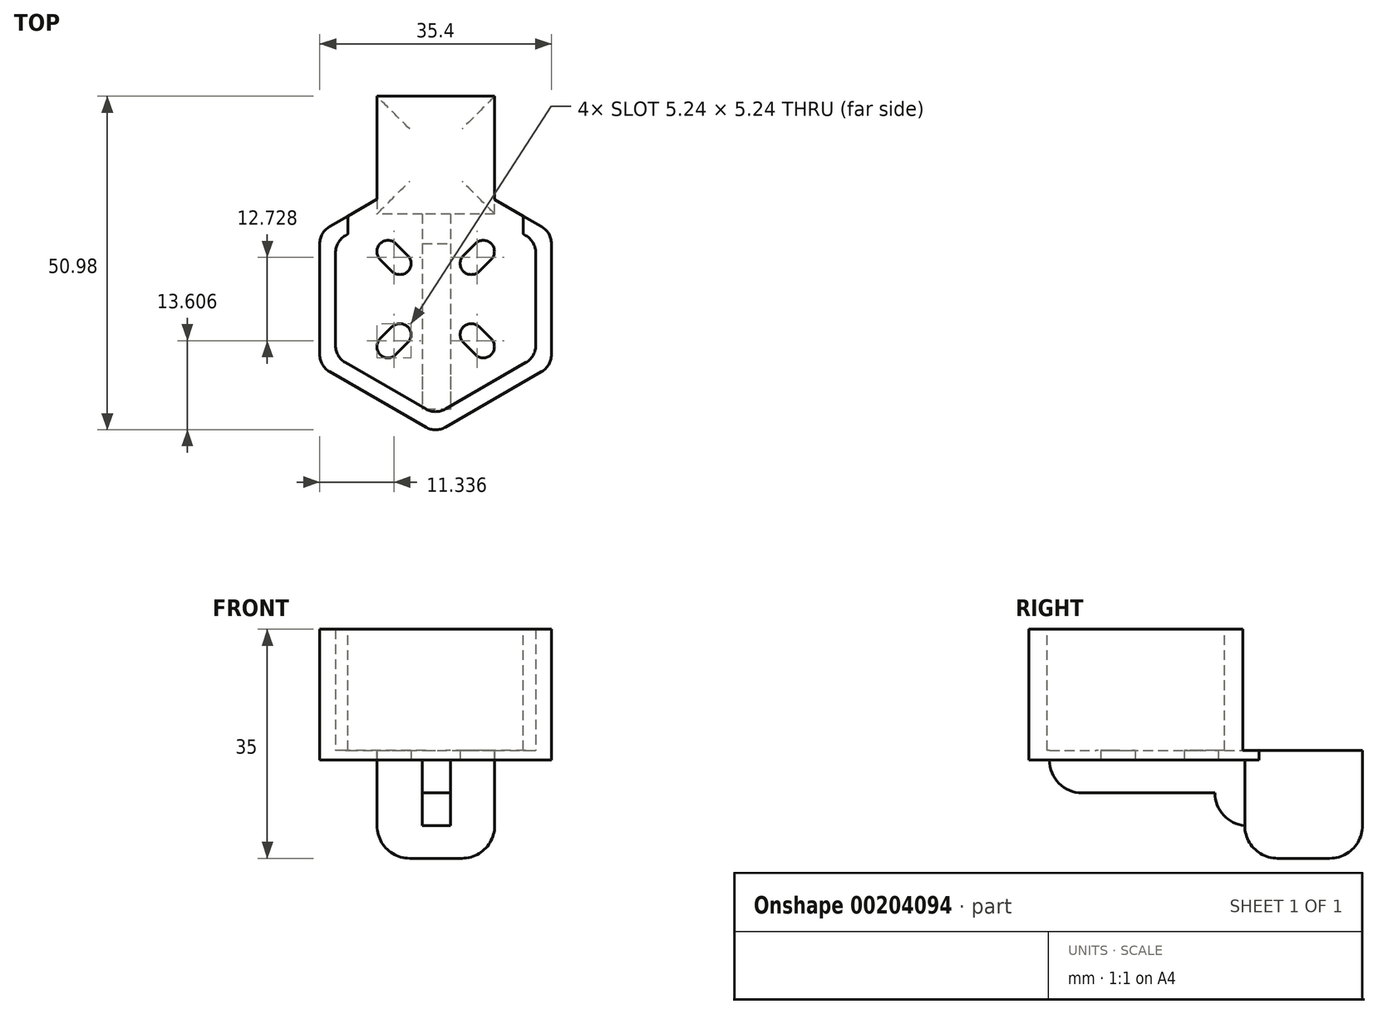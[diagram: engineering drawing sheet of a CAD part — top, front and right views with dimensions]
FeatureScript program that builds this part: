
annotation { "Feature Type Name" : "Feature", "Feature Type Description" : "" }
export const myFeature = defineFeature(function(context is Context, id is Id, definition is map)
    precondition{}
    {
        {
            var Q0;
            Q0=qCreatedBy(makeId("Top.planeOp"),FACE);
            var sketch = newSketch(context, id + "F0", { "sketchPlane" : qUnion([Q0])});
            skPoint(sketch, "E0", {"position": v(0, 0) * mm});
            skLineSegment(sketch, "E1", {"start": v(-20.56, -20.56) * mm, "end": v(20.56, 20.56) * mm, "construction": true});
            skLineSegment(sketch, "E2", {"start": v(-19.47, 19.47) * mm, "end": v(19.47, -19.47) * mm, "construction": true});
            skArc(sketch, "E3", {"start": v(-6.08, 8.49) * mm, "mid": v(-8.49, 8.49) * mm, "end": v(-8.49, 6.08) * mm});
            skArc(sketch, "E4", {"start": v(-6.65, 4.24) * mm, "mid": v(-4.24, 4.24) * mm, "end": v(-4.24, 6.65) * mm});
            skLineSegment(sketch, "E5", {"start": v(-6.08, 8.49) * mm, "end": v(-4.24, 6.65) * mm});
            skLineSegment(sketch, "E6", {"start": v(-8.49, 6.08) * mm, "end": v(-6.65, 4.24) * mm});
            skLineSegment(sketch, "E7.MirrorCS", {"start": v(-8.49, -6.08) * mm, "end": v(-6.65, -4.24) * mm});
            skArc(sketch, "E8.MirrorCS", {"start": v(-6.08, -8.49) * mm, "mid": v(-8.49, -8.49) * mm, "end": v(-8.49, -6.08) * mm});
            skArc(sketch, "E9.MirrorCS", {"start": v(-6.65, -4.24) * mm, "mid": v(-4.24, -4.24) * mm, "end": v(-4.24, -6.65) * mm});
            skLineSegment(sketch, "E10.MirrorCS", {"start": v(-6.08, -8.49) * mm, "end": v(-4.24, -6.65) * mm});
            skLineSegment(sketch, "E11.MirrorCS", {"start": v(6.08, -8.49) * mm, "end": v(4.24, -6.65) * mm});
            skLineSegment(sketch, "E12.MirrorCS", {"start": v(8.49, -6.08) * mm, "end": v(6.65, -4.24) * mm});
            skLineSegment(sketch, "E13.MirrorCS", {"start": v(6.08, 8.49) * mm, "end": v(4.24, 6.65) * mm});
            skArc(sketch, "E14.MirrorCS", {"start": v(6.65, -4.24) * mm, "mid": v(4.24, -4.24) * mm, "end": v(4.24, -6.65) * mm});
            skLineSegment(sketch, "E15.MirrorCS", {"start": v(8.49, 6.08) * mm, "end": v(6.65, 4.24) * mm});
            skArc(sketch, "E16.MirrorCS", {"start": v(6.08, -8.49) * mm, "mid": v(8.49, -8.49) * mm, "end": v(8.49, -6.08) * mm});
            skArc(sketch, "E17.MirrorCS", {"start": v(6.08, 8.49) * mm, "mid": v(8.49, 8.49) * mm, "end": v(8.49, 6.08) * mm});
            skArc(sketch, "E18.MirrorCS", {"start": v(6.65, 4.24) * mm, "mid": v(4.24, 4.24) * mm, "end": v(4.24, 6.65) * mm});
            skCircle(sketch, "E19.cCircle", {"center": v(0, 0) * mm, "radius": 15.3 * mm, "construction": true});
            skLineSegment(sketch, "E19.0", {"start": v(15.3, -8.83) * mm, "end": v(0, -17.67) * mm});
            skLineSegment(sketch, "E19.1", {"start": v(0, -17.67) * mm, "end": v(-15.3, -8.83) * mm});
            skLineSegment(sketch, "E19.2", {"start": v(-15.3, -8.83) * mm, "end": v(-15.3, 8.83) * mm});
            skLineSegment(sketch, "E19.3", {"start": v(-15.3, 8.83) * mm, "end": v(0, 17.67) * mm});
            skLineSegment(sketch, "E19.4", {"start": v(0, 17.67) * mm, "end": v(15.3, 8.83) * mm});
            skLineSegment(sketch, "E19.5", {"start": v(15.3, 8.83) * mm, "end": v(15.3, -8.83) * mm});
            skPoint(sketch, "E19.0.midPoint", {"position": v(7.65, -13.25) * mm});
            skLineSegment(sketch, "E20.0", {"start": v(-17.7, -10.22) * mm, "end": v(-17.7, 10.22) * mm});
            skLineSegment(sketch, "E20.1", {"start": v(0, 20.44) * mm, "end": v(17.7, 10.22) * mm});
            skLineSegment(sketch, "E20.2", {"start": v(17.7, 10.22) * mm, "end": v(17.7, -10.22) * mm});
            skLineSegment(sketch, "E20.3", {"start": v(-17.7, 10.22) * mm, "end": v(0, 20.44) * mm});
            skLineSegment(sketch, "E20.4", {"start": v(17.7, -10.22) * mm, "end": v(0, -20.44) * mm});
            skLineSegment(sketch, "E20.5", {"start": v(0, -20.44) * mm, "end": v(-17.7, -10.22) * mm});
            skSolve(sketch);
        }
        {
            var Q0;
            Q0=makeQuery(id+"F0.imprint","IMPRINT",FACE,{"disambiguationData":[TD([[makeQuery(id+"F0.imprint","IMPRINT",EDGE,{"derivedFrom":sQuery(id+"F0.wireOp",EDGE,"E3")}),-1.0]])]});
            extrude(context, id + "F1", {"entities" : qUnion([Q0]), "depth" : 1.5 * mm});
        }
        {
            var Q0;
            Q0=makeQuery(id+"F0.imprint","IMPRINT",FACE,{"disambiguationData":[TD([[makeQuery(id+"F0.imprint","IMPRINT",EDGE,{"derivedFrom":sQuery(id+"F0.wireOp",EDGE,"E19.0")}),1.0]])]});
            extrude(context, id + "F2", {"entities" : qUnion([Q0]), "operationType" : NewBodyOperationType.ADD, "depth" : 20 * mm});
        }
        {
            var Q0;
            Q0=qCreatedBy(makeId("Front.planeOp"),FACE);
            cPlane(context, id + "F3", {"entities" : qUnion([Q0]), "cplaneType" : CPlaneType.OFFSET, "offset" : 25 * mm, "oppositeDirection" : true, "width" : 150 * mm, "height" : 150 * mm});
        }
        {
            var Q0;
            Q0=qCreatedBy(id+"F3.planeOp",FACE);
            var sketch = newSketch(context, id + "F4", { "sketchPlane" : qUnion([Q0])});
            skLineSegment(sketch, "E21.bottom", {"start": v(-13.4, 1.5) * mm, "end": v(13.4, 1.5) * mm});
            skLineSegment(sketch, "E21.top", {"start": v(-13.4, 21.94) * mm, "end": v(13.4, 21.94) * mm});
            skLineSegment(sketch, "E21.left", {"start": v(-13.4, 1.5) * mm, "end": v(-13.4, 21.94) * mm});
            skLineSegment(sketch, "E21.right", {"start": v(13.4, 1.5) * mm, "end": v(13.4, 21.94) * mm});
            skPoint(sketch, "E21.middle", {"position": v(0, 11.72) * mm});
            skSolve(sketch);
        }
        {
            var Q0;
            Q0=makeQuery(id+"F4.imprint","IMPRINT",FACE,{"disambiguationData":[TD([[makeQuery(id+"F4.imprint","IMPRINT",EDGE,{"derivedFrom":sQuery(id+"F4.wireOp",EDGE,"E21.bottom")}),1.0]])]});
            extrude(context, id + "F5", {"entities" : qUnion([Q0]), "operationType" : NewBodyOperationType.REMOVE, "depth" : 26 * mm});
        }
        {
            var Q0;
            Q0=makeQuery(id+"F2.opExtrude","SWEPT_EDGE",EDGE,{"disambiguationData":[OSD([sQuery(id+"F0.wireOp",EDGE,"E20.1"),sQuery(id+"F0.wireOp",EDGE,"E20.2")])]});
            var Q1;
            Q1=makeQuery(id+"F2.opExtrude","SWEPT_EDGE",EDGE,{"disambiguationData":[OSD([sQuery(id+"F0.wireOp",EDGE,"E20.0"),sQuery(id+"F0.wireOp",EDGE,"E20.3")])]});
            var Q2;
            Q2=makeQuery(id+"F2.opExtrude","SWEPT_EDGE",EDGE,{"disambiguationData":[OSD([sQuery(id+"F0.wireOp",EDGE,"E20.0"),sQuery(id+"F0.wireOp",EDGE,"E20.5")])]});
            var Q3;
            Q3=makeQuery(id+"F2.opExtrude","SWEPT_EDGE",EDGE,{"disambiguationData":[OSD([sQuery(id+"F0.wireOp",EDGE,"E20.4"),sQuery(id+"F0.wireOp",EDGE,"E20.5")])]});
            var Q4;
            Q4=makeQuery(id+"F2.opExtrude","SWEPT_EDGE",EDGE,{"disambiguationData":[OSD([sQuery(id+"F0.wireOp",EDGE,"E20.2"),sQuery(id+"F0.wireOp",EDGE,"E20.4")])]});
            var Q5;
            Q5=makeQuery(id+"F2.opExtrude","SWEPT_EDGE",EDGE,{"disambiguationData":[OSD([sQuery(id+"F0.wireOp",EDGE,"E19.4"),sQuery(id+"F0.wireOp",EDGE,"E19.5")])]});
            var Q6;
            Q6=makeQuery(id+"F2.opExtrude","SWEPT_EDGE",EDGE,{"disambiguationData":[OSD([sQuery(id+"F0.wireOp",EDGE,"E19.0"),sQuery(id+"F0.wireOp",EDGE,"E19.5")])]});
            var Q7;
            Q7=makeQuery(id+"F2.opExtrude","SWEPT_EDGE",EDGE,{"disambiguationData":[OSD([sQuery(id+"F0.wireOp",EDGE,"E19.0"),sQuery(id+"F0.wireOp",EDGE,"E19.1")])]});
            var Q8;
            Q8=makeQuery(id+"F2.opExtrude","SWEPT_EDGE",EDGE,{"disambiguationData":[OSD([sQuery(id+"F0.wireOp",EDGE,"E19.1"),sQuery(id+"F0.wireOp",EDGE,"E19.2")])]});
            var Q9;
            Q9=makeQuery(id+"F2.opExtrude","SWEPT_EDGE",EDGE,{"disambiguationData":[OSD([sQuery(id+"F0.wireOp",EDGE,"E19.2"),sQuery(id+"F0.wireOp",EDGE,"E19.3")])]});
            fillet(context, id + "F6", {"entities" : qUnion([Q0, Q1, Q2, Q3, Q4, Q5, Q6, Q7, Q8, Q9]), "radius" : 3 * mm, "tangentPropagation" : true, "allowEdgeOverflow" : false});
        }
        {
            var Q0;
            Q0=makeQuery(id+"F1.opExtrude","CAP_EDGE",EDGE,{"disambiguationData":[OSD([sQuery(id+"F0.wireOp",EDGE,"E19.3")])],"isStart":false});
            var Q1;
            Q1=makeQuery(id+"F2.opExtrude","SWEPT_EDGE",EDGE,{"disambiguationData":[OSD([sQuery(id+"F0.wireOp",EDGE,"E20.1"),sQuery(id+"F0.wireOp",EDGE,"E20.3")])]});
            fillet(context, id + "F7", {"entities" : qUnion([Q0, Q1]), "radius" : 0.5 * mm, "tangentPropagation" : true, "allowEdgeOverflow" : false});
        }
        {
            var Q0;
            Q0=makeQuery(id+"F5.boolean.opBoolean","MERGE",FACE,{"derivedFrom":[makeQuery(id+"F1.opExtrude","CAP_FACE",FACE,{"disambiguationData":[OSD([sQuery(id+"F0.wireOp",EDGE,"E3"),sQuery(id+"F0.wireOp",EDGE,"E4"),sQuery(id+"F0.wireOp",EDGE,"E5"),sQuery(id+"F0.wireOp",EDGE,"E6"),sQuery(id+"F0.wireOp",EDGE,"E7.MirrorCS"),sQuery(id+"F0.wireOp",EDGE,"E8.MirrorCS"),sQuery(id+"F0.wireOp",EDGE,"E9.MirrorCS"),sQuery(id+"F0.wireOp",EDGE,"E10.MirrorCS"),sQuery(id+"F0.wireOp",EDGE,"E11.MirrorCS"),sQuery(id+"F0.wireOp",EDGE,"E12.MirrorCS"),sQuery(id+"F0.wireOp",EDGE,"E13.MirrorCS"),sQuery(id+"F0.wireOp",EDGE,"E14.MirrorCS"),sQuery(id+"F0.wireOp",EDGE,"E15.MirrorCS"),sQuery(id+"F0.wireOp",EDGE,"E16.MirrorCS"),sQuery(id+"F0.wireOp",EDGE,"E17.MirrorCS"),sQuery(id+"F0.wireOp",EDGE,"E18.MirrorCS"),sQuery(id+"F0.wireOp",EDGE,"E19.0"),sQuery(id+"F0.wireOp",EDGE,"E19.1"),sQuery(id+"F0.wireOp",EDGE,"E19.2"),sQuery(id+"F0.wireOp",EDGE,"E19.3"),sQuery(id+"F0.wireOp",EDGE,"E19.4"),sQuery(id+"F0.wireOp",EDGE,"E19.5")])],"isStart":false}),makeQuery(id+"F5.opExtrude","SWEPT_FACE",FACE,{"disambiguationData":[OSD([sQuery(id+"F4.wireOp",EDGE,"E21.bottom")])]})]});
            var sketch = newSketch(context, id + "F8", { "sketchPlane" : qUnion([Q0])});
            skLineSegment(sketch, "E22.bottom", {"start": v(-8.97, 11.01) * mm, "end": v(9.03, 11.01) * mm});
            skLineSegment(sketch, "E22.top", {"start": v(-8.97, 31.01) * mm, "end": v(9.03, 31.01) * mm});
            skLineSegment(sketch, "E22.left", {"start": v(-8.97, 11.01) * mm, "end": v(-8.97, 31.01) * mm});
            skLineSegment(sketch, "E22.right", {"start": v(9.03, 11.01) * mm, "end": v(9.03, 31.01) * mm});
            skSolve(sketch);
        }
        {
            var Q0;
            {var subQ5=sQuery(id+"F8.wireOp",EDGE,"E22.top");Q0=makeQuery(id+"F8.imprint","IMPRINT",FACE,{"disambiguationData":[TD([[makeQuery(id+"F8.imprint","IMPRINT",EDGE,{"derivedFrom":subQ5}),-1.0]])]});}
            extrude(context, id + "F9", {"entities" : qUnion([Q0]), "operationType" : NewBodyOperationType.ADD, "oppositeDirection" : true, "depth" : 1.5 * mm});
        }
        {
            var Q0;
            {var subQ0=sQuery(id+"F0.wireOp",EDGE,"E20.3");var subQ1=sQuery(id+"F0.wireOp",EDGE,"E20.1");var subQ2=sQuery(id+"F0.wireOp",EDGE,"E19.5");var subQ3=sQuery(id+"F0.wireOp",EDGE,"E19.4");var subQ4=sQuery(id+"F0.wireOp",EDGE,"E19.3");var subQ5=sQuery(id+"F0.wireOp",EDGE,"E19.2");var subQ6=sQuery(id+"F0.wireOp",EDGE,"E19.1");var subQ7=sQuery(id+"F0.wireOp",EDGE,"E19.0");var subQ8=sQuery(id+"F0.wireOp",EDGE,"E18.MirrorCS");var subQ9=sQuery(id+"F0.wireOp",EDGE,"E17.MirrorCS");var subQ10=sQuery(id+"F0.wireOp",EDGE,"E16.MirrorCS");var subQ11=sQuery(id+"F0.wireOp",EDGE,"E15.MirrorCS");var subQ12=sQuery(id+"F0.wireOp",EDGE,"E14.MirrorCS");var subQ13=sQuery(id+"F0.wireOp",EDGE,"E13.MirrorCS");var subQ14=sQuery(id+"F0.wireOp",EDGE,"E12.MirrorCS");var subQ15=sQuery(id+"F0.wireOp",EDGE,"E11.MirrorCS");var subQ16=sQuery(id+"F0.wireOp",EDGE,"E10.MirrorCS");var subQ17=sQuery(id+"F0.wireOp",EDGE,"E9.MirrorCS");var subQ18=sQuery(id+"F0.wireOp",EDGE,"E8.MirrorCS");var subQ19=sQuery(id+"F0.wireOp",EDGE,"E7.MirrorCS");var subQ20=sQuery(id+"F0.wireOp",EDGE,"E6");var subQ21=sQuery(id+"F0.wireOp",EDGE,"E5");var subQ22=sQuery(id+"F0.wireOp",EDGE,"E4");var subQ23=sQuery(id+"F0.wireOp",EDGE,"E3");Q0=makeQuery(id+"F9.boolean.opBoolean","MERGE",FACE,{"derivedFrom":[makeQuery(id+"F2.boolean.opBoolean","MERGE",FACE,{"derivedFrom":[makeQuery(id+"F1.opExtrude","CAP_FACE",FACE,{"disambiguationData":[OSD([subQ23,subQ22,subQ21,subQ20,subQ19,subQ18,subQ17,subQ16,subQ15,subQ14,subQ13,subQ12,subQ11,subQ10,subQ9,subQ8,subQ7,subQ6,subQ5,subQ4,subQ3,subQ2])],"isStart":true}),makeQuery(id+"F2.opExtrude","CAP_FACE",FACE,{"disambiguationData":[OSD([subQ7,subQ6,subQ5,subQ4,subQ3,subQ2,sQuery(id+"F0.wireOp",EDGE,"E20.0"),subQ1,sQuery(id+"F0.wireOp",EDGE,"E20.2"),subQ0,sQuery(id+"F0.wireOp",EDGE,"E20.4"),sQuery(id+"F0.wireOp",EDGE,"E20.5")])],"isStart":true})]}),makeQuery(id+"F9.opExtrude","CAP_FACE",FACE,{"disambiguationData":[OSD([subQ23,subQ22,subQ21,subQ20,subQ19,subQ18,subQ17,subQ16,subQ15,subQ14,subQ13,subQ12,subQ11,subQ10,subQ9,subQ8,subQ7,subQ6,subQ5,subQ4,subQ3,subQ2,subQ1,subQ0,sQuery(id+"F4.wireOp",EDGE,"E21.bottom"),sQuery(id+"F8.wireOp",EDGE,"E22.top"),sQuery(id+"F8.wireOp",EDGE,"E22.left"),sQuery(id+"F8.wireOp",EDGE,"E22.right")])],"isStart":false})]});}
            var sketch = newSketch(context, id + "F10", { "sketchPlane" : qUnion([Q0])});
            skLineSegment(sketch, "E23.bottom", {"start": v(9.03, -31.01) * mm, "end": v(-8.97, -31.01) * mm});
            skLineSegment(sketch, "E23.top", {"start": v(9.03, -13.01) * mm, "end": v(-8.97, -13.01) * mm});
            skLineSegment(sketch, "E23.left", {"start": v(9.03, -31.01) * mm, "end": v(9.03, -13.01) * mm});
            skLineSegment(sketch, "E23.right", {"start": v(-8.97, -31.01) * mm, "end": v(-8.97, -13.01) * mm});
            skSolve(sketch);
        }
        {
            var Q0;
            Q0 = qSketchRegion(id + "F10", true);
            extrude(context, id + "F11", {"entities" : qUnion([Q0]), "operationType" : NewBodyOperationType.ADD, "depth" : 15 * mm});
        }
        {
            var Q0;
            Q0=makeQuery(id+"F11.opExtrude","CAP_EDGE",EDGE,{"disambiguationData":[OSD([sQuery(id+"F10.wireOp",EDGE,"E23.left")])],"isStart":false});
            var Q1;
            Q1=makeQuery(id+"F11.opExtrude","CAP_EDGE",EDGE,{"disambiguationData":[OSD([sQuery(id+"F10.wireOp",EDGE,"E23.top")])],"isStart":false});
            var Q2;
            Q2=makeQuery(id+"F11.opExtrude","CAP_EDGE",EDGE,{"disambiguationData":[OSD([sQuery(id+"F10.wireOp",EDGE,"E23.right")])],"isStart":false});
            var Q3;
            Q3=makeQuery(id+"F11.opExtrude","CAP_EDGE",EDGE,{"disambiguationData":[OSD([sQuery(id+"F10.wireOp",EDGE,"E23.bottom")])],"isStart":false});
            fillet(context, id + "F12", {"entities" : qUnion([Q0, Q1, Q2, Q3]), "radius" : 5 * mm, "tangentPropagation" : true, "allowEdgeOverflow" : false});
        }
        {
            var Q0;
            {var subQ0=sQuery(id+"F0.wireOp",EDGE,"E20.3");var subQ1=sQuery(id+"F0.wireOp",EDGE,"E20.1");var subQ2=sQuery(id+"F0.wireOp",EDGE,"E19.5");var subQ3=sQuery(id+"F0.wireOp",EDGE,"E19.4");var subQ4=sQuery(id+"F0.wireOp",EDGE,"E19.3");var subQ5=sQuery(id+"F0.wireOp",EDGE,"E19.2");var subQ6=sQuery(id+"F0.wireOp",EDGE,"E19.1");var subQ7=sQuery(id+"F0.wireOp",EDGE,"E19.0");var subQ8=sQuery(id+"F0.wireOp",EDGE,"E18.MirrorCS");var subQ9=sQuery(id+"F0.wireOp",EDGE,"E17.MirrorCS");var subQ10=sQuery(id+"F0.wireOp",EDGE,"E16.MirrorCS");var subQ11=sQuery(id+"F0.wireOp",EDGE,"E15.MirrorCS");var subQ12=sQuery(id+"F0.wireOp",EDGE,"E14.MirrorCS");var subQ13=sQuery(id+"F0.wireOp",EDGE,"E13.MirrorCS");var subQ14=sQuery(id+"F0.wireOp",EDGE,"E12.MirrorCS");var subQ15=sQuery(id+"F0.wireOp",EDGE,"E11.MirrorCS");var subQ16=sQuery(id+"F0.wireOp",EDGE,"E10.MirrorCS");var subQ17=sQuery(id+"F0.wireOp",EDGE,"E9.MirrorCS");var subQ18=sQuery(id+"F0.wireOp",EDGE,"E8.MirrorCS");var subQ19=sQuery(id+"F0.wireOp",EDGE,"E7.MirrorCS");var subQ20=sQuery(id+"F0.wireOp",EDGE,"E6");var subQ21=sQuery(id+"F0.wireOp",EDGE,"E5");var subQ22=sQuery(id+"F0.wireOp",EDGE,"E4");var subQ23=sQuery(id+"F0.wireOp",EDGE,"E3");Q0=makeQuery(id+"F9.boolean.opBoolean","MERGE",FACE,{"derivedFrom":[makeQuery(id+"F2.boolean.opBoolean","MERGE",FACE,{"derivedFrom":[makeQuery(id+"F1.opExtrude","CAP_FACE",FACE,{"disambiguationData":[OSD([subQ23,subQ22,subQ21,subQ20,subQ19,subQ18,subQ17,subQ16,subQ15,subQ14,subQ13,subQ12,subQ11,subQ10,subQ9,subQ8,subQ7,subQ6,subQ5,subQ4,subQ3,subQ2])],"isStart":true}),makeQuery(id+"F2.opExtrude","CAP_FACE",FACE,{"disambiguationData":[OSD([subQ7,subQ6,subQ5,subQ4,subQ3,subQ2,sQuery(id+"F0.wireOp",EDGE,"E20.0"),subQ1,sQuery(id+"F0.wireOp",EDGE,"E20.2"),subQ0,sQuery(id+"F0.wireOp",EDGE,"E20.4"),sQuery(id+"F0.wireOp",EDGE,"E20.5")])],"isStart":true})]}),makeQuery(id+"F9.opExtrude","CAP_FACE",FACE,{"disambiguationData":[OSD([subQ23,subQ22,subQ21,subQ20,subQ19,subQ18,subQ17,subQ16,subQ15,subQ14,subQ13,subQ12,subQ11,subQ10,subQ9,subQ8,subQ7,subQ6,subQ5,subQ4,subQ3,subQ2,subQ1,subQ0,sQuery(id+"F4.wireOp",EDGE,"E21.bottom"),sQuery(id+"F8.wireOp",EDGE,"E22.top"),sQuery(id+"F8.wireOp",EDGE,"E22.left"),sQuery(id+"F8.wireOp",EDGE,"E22.right")])],"isStart":false})]});}
            var sketch = newSketch(context, id + "F13", { "sketchPlane" : qUnion([Q0])});
            skLineSegment(sketch, "E24.bottom", {"start": v(2.29, -13.01) * mm, "end": v(-2.03, -13.01) * mm});
            skLineSegment(sketch, "E24.top", {"start": v(2.29, 16.84) * mm, "end": v(-2.03, 16.84) * mm});
            skLineSegment(sketch, "E24.left", {"start": v(2.29, -13.01) * mm, "end": v(2.29, 16.84) * mm});
            skLineSegment(sketch, "E24.right", {"start": v(-2.03, -13.01) * mm, "end": v(-2.03, 16.84) * mm});
            skSolve(sketch);
        }
        {
            var Q0;
            Q0 = qSketchRegion(id + "F13", true);
            extrude(context, id + "F14", {"entities" : qUnion([Q0]), "operationType" : NewBodyOperationType.ADD, "depth" : 5 * mm});
        }
        {
            var Q0;
            Q0=makeQuery(id+"F14.opExtrude","CAP_EDGE",EDGE,{"disambiguationData":[OSD([sQuery(id+"F13.wireOp",EDGE,"E24.top")])],"isStart":false});
            fillet(context, id + "F15", {"entities" : qUnion([Q0]), "radius" : 5 * mm, "tangentPropagation" : true, "allowEdgeOverflow" : false});
        }
        {
            var Q0;
            Q0=makeQuery(id+"F14.opExtrude","CAP_FACE",FACE,{"disambiguationData":[OSD([sQuery(id+"F13.wireOp",EDGE,"E24.bottom"),sQuery(id+"F13.wireOp",EDGE,"E24.top"),sQuery(id+"F13.wireOp",EDGE,"E24.left"),sQuery(id+"F13.wireOp",EDGE,"E24.right")])],"isStart":false});
            var sketch = newSketch(context, id + "F16", { "sketchPlane" : qUnion([Q0])});
            skLineSegment(sketch, "E25.bottom", {"start": v(-2.03, -8.46) * mm, "end": v(2.29, -8.46) * mm});
            skLineSegment(sketch, "E25.top", {"start": v(-2.03, -13.01) * mm, "end": v(2.29, -13.01) * mm});
            skLineSegment(sketch, "E25.left", {"start": v(-2.03, -8.46) * mm, "end": v(-2.03, -13.01) * mm});
            skLineSegment(sketch, "E25.right", {"start": v(2.29, -8.46) * mm, "end": v(2.29, -13.01) * mm});
            skSolve(sketch);
        }
        {
            var Q0;
            Q0 = qSketchRegion(id + "F16", true);
            extrude(context, id + "F17", {"entities" : qUnion([Q0]), "operationType" : NewBodyOperationType.ADD, "depth" : 5 * mm});
        }
        {
            var Q0;
            Q0=makeQuery(id+"F17.opExtrude","CAP_EDGE",EDGE,{"disambiguationData":[OSD([sQuery(id+"F16.wireOp",EDGE,"E25.bottom")])],"isStart":false});
            fillet(context, id + "F18", {"entities" : qUnion([Q0]), "radius" : 5 * mm, "tangentPropagation" : true, "allowEdgeOverflow" : false});
        }
    });
